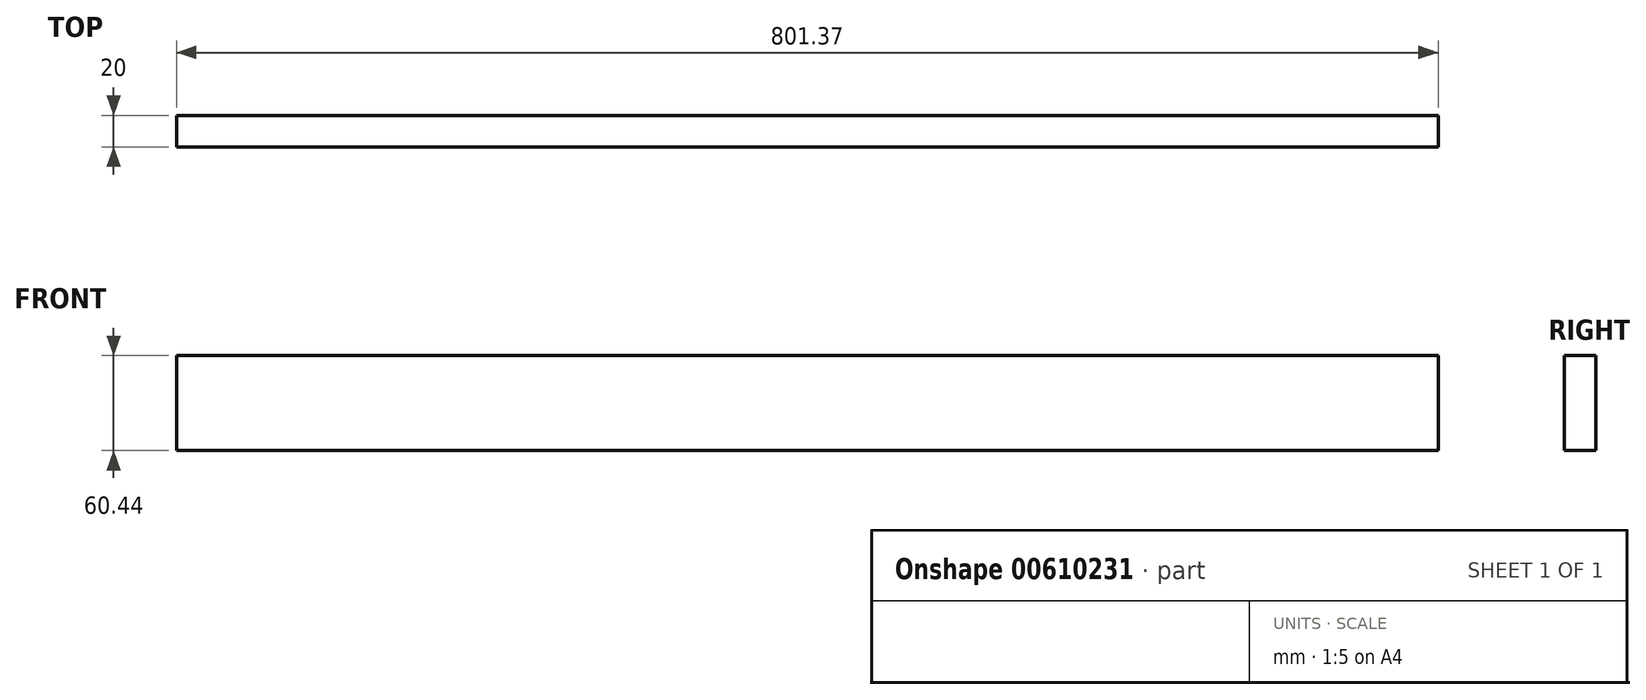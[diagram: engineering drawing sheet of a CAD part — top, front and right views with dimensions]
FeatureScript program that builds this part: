
annotation { "Feature Type Name" : "Feature", "Feature Type Description" : "" }
export const myFeature = defineFeature(function(context is Context, id is Id, definition is map)
    precondition{}
    {
        {
            var Q0;
            Q0=qCreatedBy(makeId("Front.planeOp"),FACE);
            var sketch = newSketch(context, id + "F0", { "sketchPlane" : qUnion([Q0])});
            skLineSegment(sketch, "E0.bottom", {"start": v(-383.2, 38.5) * mm, "end": v(418.18, 38.5) * mm});
            skLineSegment(sketch, "E0.top", {"start": v(-383.2, -21.94) * mm, "end": v(418.18, -21.94) * mm});
            skLineSegment(sketch, "E0.left", {"start": v(-383.2, 38.5) * mm, "end": v(-383.2, -21.94) * mm});
            skLineSegment(sketch, "E0.right", {"start": v(418.18, 38.5) * mm, "end": v(418.18, -21.94) * mm});
            skSolve(sketch);
        }
        {
            var Q0;
            Q0=makeQuery(id+"F0.imprint","IMPRINT",FACE,{"disambiguationData":[TD([[makeQuery(id+"F0.imprint","IMPRINT",EDGE,{"derivedFrom":sQuery(id+"F0.wireOp",EDGE,"E0.bottom")}),-1.0]])]});
            extrude(context, id + "F1", {"entities" : qUnion([Q0]), "depth" : 20 * mm, "offsetDistance" : 25.4 * mm});
        }
    });
